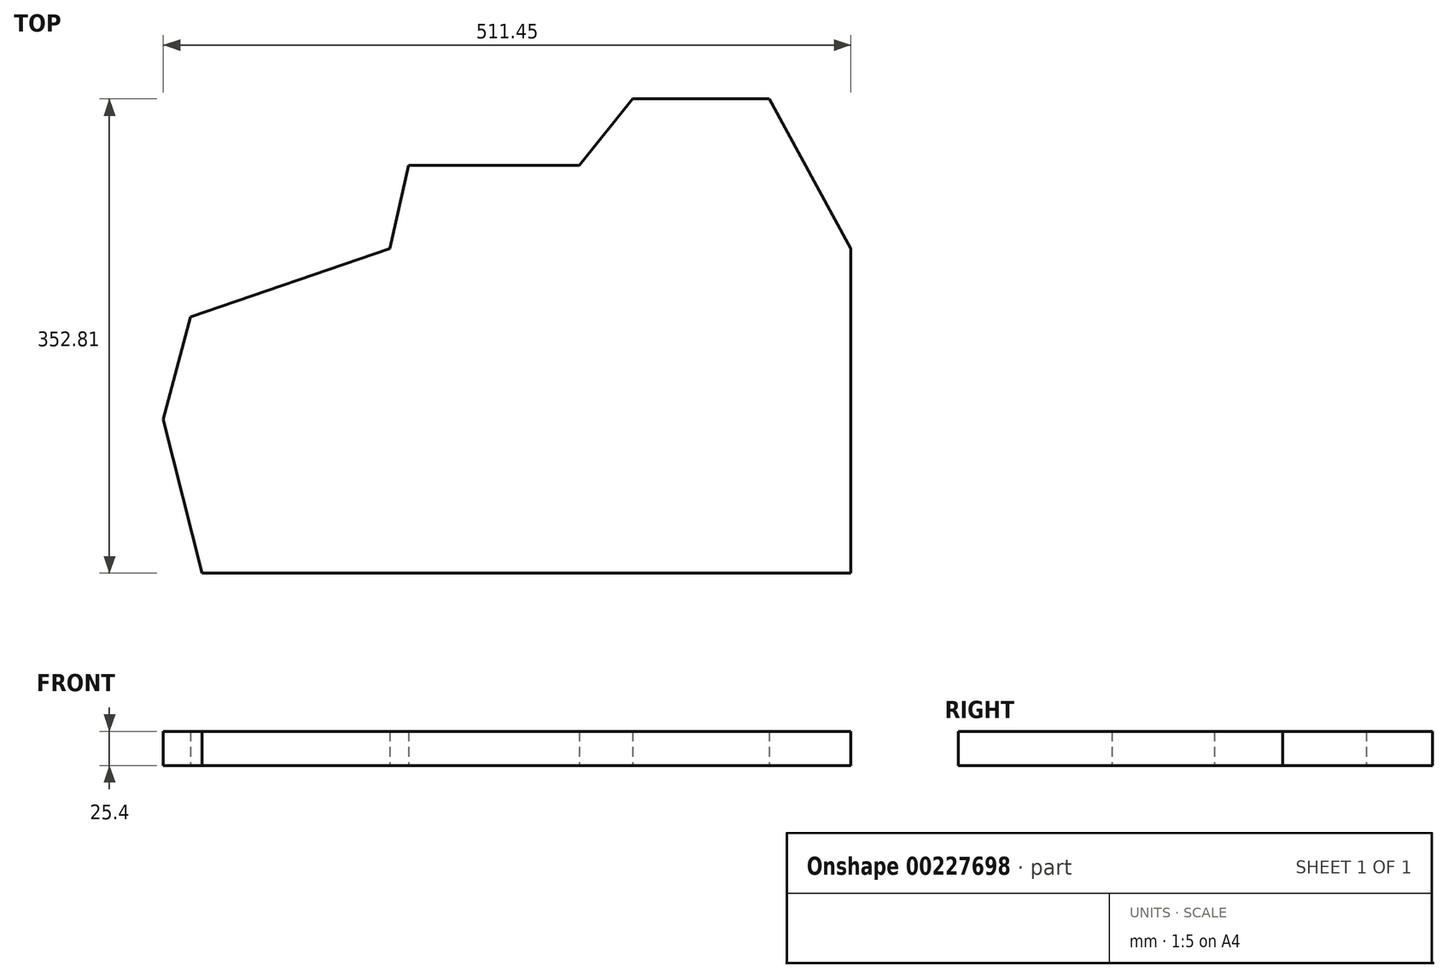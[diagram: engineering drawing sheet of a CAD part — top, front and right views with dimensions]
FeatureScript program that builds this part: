
annotation { "Feature Type Name" : "Feature", "Feature Type Description" : "" }
export const myFeature = defineFeature(function(context is Context, id is Id, definition is map)
    precondition{}
    {
        {
            var Q0;
            Q0=qCreatedBy(makeId("Top.planeOp"),FACE);
            var sketch = newSketch(context, id + "F0", { "sketchPlane" : qUnion([Q0])});
            skLineSegment(sketch, "E0", {"start": v(-215.48, 0) * mm, "end": v(-186.63, -114.3) * mm});
            skLineSegment(sketch, "E1", {"start": v(-186.63, -114.3) * mm, "end": v(295.97, -114.3) * mm});
            skLineSegment(sketch, "E2", {"start": v(295.97, -114.3) * mm, "end": v(295.97, 127) * mm});
            skLineSegment(sketch, "E3", {"start": v(295.97, 127) * mm, "end": v(235.18, 238.5) * mm});
            skLineSegment(sketch, "E4", {"start": v(235.18, 238.5) * mm, "end": v(133.58, 238.5) * mm});
            skLineSegment(sketch, "E5", {"start": v(133.58, 238.5) * mm, "end": v(93.81, 189) * mm});
            skLineSegment(sketch, "E6", {"start": v(93.81, 189) * mm, "end": v(-33.19, 189) * mm});
            skLineSegment(sketch, "E7", {"start": v(-33.19, 189) * mm, "end": v(-46.92, 127) * mm});
            skLineSegment(sketch, "E8", {"start": v(-46.92, 127) * mm, "end": v(-195.3, 76.2) * mm});
            skLineSegment(sketch, "E9", {"start": v(-195.3, 76.2) * mm, "end": v(-215.48, 0) * mm});
            skPoint(sketch, "E10", {"position": v(-46.92, 127) * mm});
            skPoint(sketch, "E11", {"position": v(0, 0) * mm});
            skPoint(sketch, "E12", {"position": v(295.97, -114.3) * mm});
            skLineSegment(sketch, "E13", {"start": v(295.97, 127) * mm, "end": v(295.97, 252.69) * mm});
            skLineSegment(sketch, "E14", {"start": v(235.18, 238.5) * mm, "end": v(235.18, 256.95) * mm});
            skSolve(sketch);
        }
        {
            var Q0;
            Q0=makeQuery(id+"F0.imprint","IMPRINT",FACE,{"disambiguationData":[TD([[makeQuery(id+"F0.imprint","IMPRINT",EDGE,{"derivedFrom":sQuery(id+"F0.wireOp",EDGE,"E0")}),1.0]])]});
            extrude(context, id + "F1", {"entities" : qUnion([Q0]), "depth" : 25.4 * mm});
        }
    });
